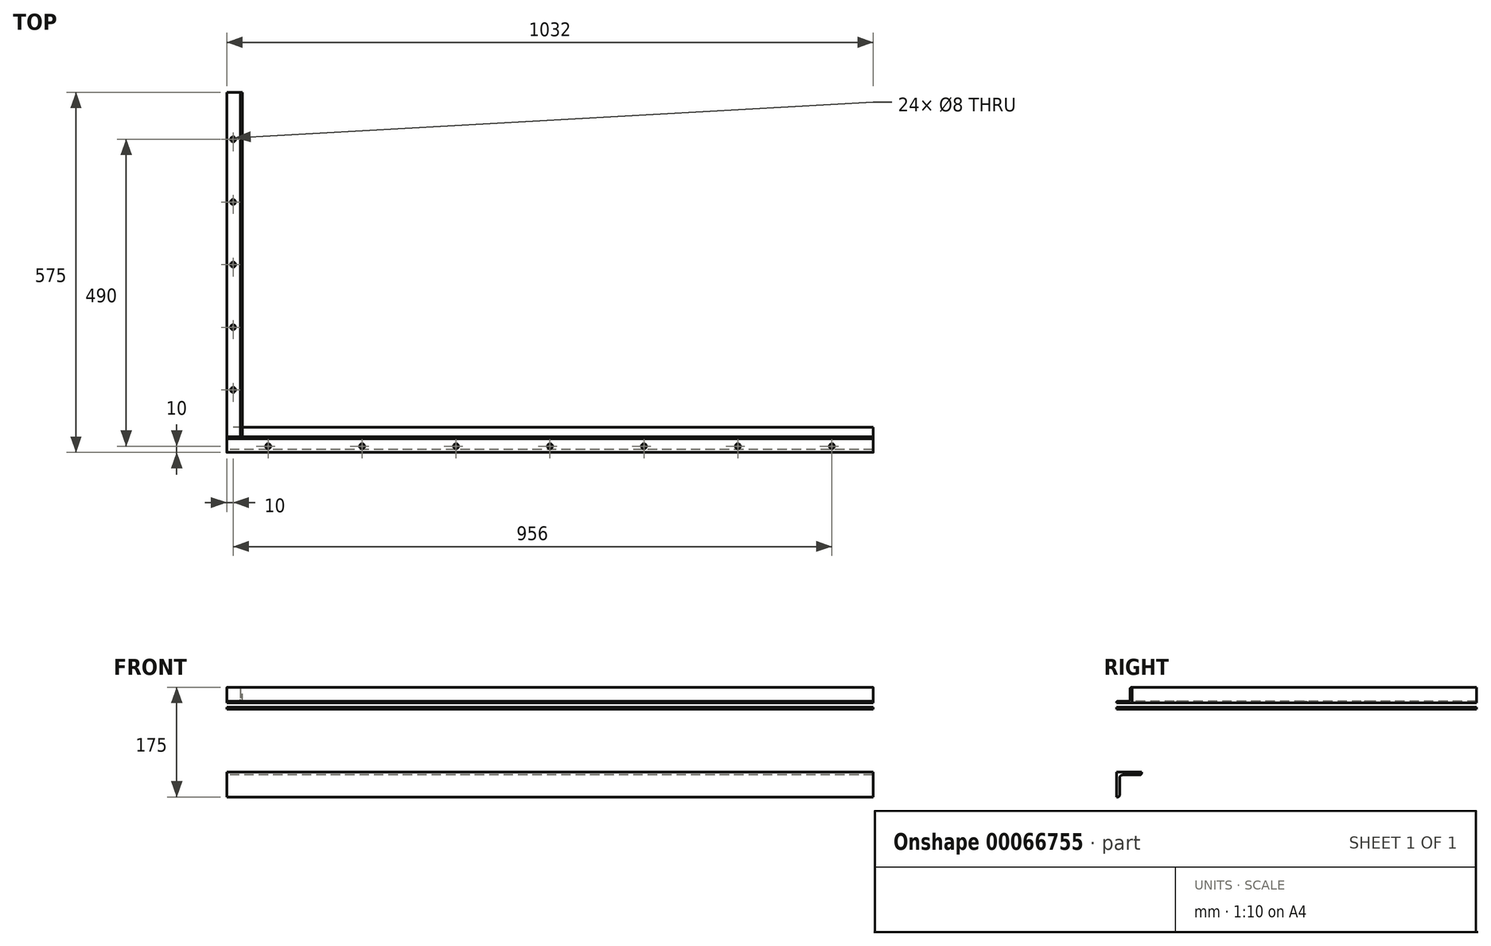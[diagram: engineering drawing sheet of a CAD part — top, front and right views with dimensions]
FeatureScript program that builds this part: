
annotation { "Feature Type Name" : "Feature", "Feature Type Description" : "" }
export const myFeature = defineFeature(function(context is Context, id is Id, definition is map)
    precondition{}
    {
        {
            assignVariable(context, id + "F0", {"name" : "E1", "anyValue" : 1032});
        }
        {
            assignVariable(context, id + "F1", {"name" : "E5", "anyValue" : 550});
        }
        {
            var Q0;
            Q0=qCreatedBy(makeId("Top.planeOp"),FACE);
            var sketch = newSketch(context, id + "F2", { "sketchPlane" : qUnion([Q0])});
            skLineSegment(sketch, "E0.bottom", {"start": v(-516, 0) * mm, "end": v(516, 0) * mm});
            skLineSegment(sketch, "E0.top", {"start": v(-516, -25) * mm, "end": v(516, -25) * mm});
            skLineSegment(sketch, "E0.left", {"start": v(-516, 0) * mm, "end": v(-516, -25) * mm});
            skLineSegment(sketch, "E0.right", {"start": v(516, 0) * mm, "end": v(516, -25) * mm});
            skLineSegment(sketch, "E1.bottom", {"start": v(-516, 550) * mm, "end": v(-491, 550) * mm});
            skLineSegment(sketch, "E1.top", {"start": v(-516, 0) * mm, "end": v(-491, 0) * mm});
            skLineSegment(sketch, "E1.left", {"start": v(-516, 550) * mm, "end": v(-516, 0) * mm});
            skLineSegment(sketch, "E1.right", {"start": v(-491, 550) * mm, "end": v(-491, 0) * mm});
            skSolve(sketch);
        }
        {
            var Q0;
            Q0=qCreatedBy(makeId("Right.planeOp"),FACE);
            var sketch = newSketch(context, id + "F3", { "sketchPlane" : qUnion([Q0])});
            skLineSegment(sketch, "E2", {"start": v(-25, 10) * mm, "end": v(0, 10) * mm});
            skLineSegment(sketch, "E3", {"start": v(0, 10) * mm, "end": v(0, 35) * mm});
            skLineSegment(sketch, "E4", {"start": v(0, 35) * mm, "end": v(-1, 35) * mm});
            skLineSegment(sketch, "E5", {"start": v(-3, 33) * mm, "end": v(-3, 16) * mm});
            skLineSegment(sketch, "E6", {"start": v(-6, 13) * mm, "end": v(-23, 13) * mm});
            skLineSegment(sketch, "E7", {"start": v(-25, 11) * mm, "end": v(-25, 10) * mm});
            skPoint(sketch, "E8.visualSharp", {"position": v(-3, 35) * mm});
            skArc(sketch, "E8.filletArc", {"start": v(-1, 35) * mm, "mid": v(-2.41, 34.41) * mm, "end": v(-3, 33) * mm});
            skPoint(sketch, "E9.visualSharp", {"position": v(-25, 13) * mm});
            skArc(sketch, "E9.filletArc", {"start": v(-23, 13) * mm, "mid": v(-24.41, 12.41) * mm, "end": v(-25, 11) * mm});
            skPoint(sketch, "E10.visualSharp", {"position": v(-3, 13) * mm});
            skArc(sketch, "E10.filletArc", {"start": v(-6, 13) * mm, "mid": v(-3.88, 13.88) * mm, "end": v(-3, 16) * mm});
            skSolve(sketch);
        }
        {
            var Q0;
            Q0=makeQuery(id+"F2.imprint","IMPRINT",FACE,{"disambiguationData":[TD([[makeQuery(id+"F2.imprint","IMPRINT",EDGE,{"derivedFrom":sQuery(id+"F2.wireOp",EDGE,"E0.bottom")}),-1.0]])]});
            extrude(context, id + "F4", {"entities" : qUnion([Q0]), "depth" : 3 * mm});
        }
        {
            var Q0;
            Q0=makeQuery(id+"F2.imprint","IMPRINT",FACE,{"disambiguationData":[TD([[makeQuery(id+"F2.imprint","IMPRINT",EDGE,{"derivedFrom":sQuery(id+"F2.wireOp",EDGE,"E1.bottom")}),-1.0]])]});
            extrude(context, id + "F5", {"entities" : qUnion([Q0]), "depth" : 3 * mm});
        }
        {
            var Q0;
            Q0=makeQuery(id+"F4.opExtrude","CAP_FACE",FACE,{"disambiguationData":[OSD([sQuery(id+"F2.wireOp",EDGE,"E0.bottom"),sQuery(id+"F2.wireOp",EDGE,"E0.top"),sQuery(id+"F2.wireOp",EDGE,"E0.left"),sQuery(id+"F2.wireOp",EDGE,"E0.right")])],"isStart":false});
            var sketch = newSketch(context, id + "F6", { "sketchPlane" : qUnion([Q0])});
            skCircle(sketch, "E11", {"center": v(-450, -15) * mm, "radius": 4 * mm});
            skCircle(sketch, "E12.1.0.0", {"center": v(-300, -15) * mm, "radius": 4 * mm});
            skCircle(sketch, "E12.2.0.0", {"center": v(-150, -15) * mm, "radius": 4 * mm});
            skCircle(sketch, "E12.3.0.0", {"center": v(0, -15) * mm, "radius": 4 * mm});
            skCircle(sketch, "E12.4.0.0", {"center": v(150, -15) * mm, "radius": 4 * mm});
            skCircle(sketch, "E12.5.0.0", {"center": v(300, -15) * mm, "radius": 4 * mm});
            skCircle(sketch, "E12.6.0.0", {"center": v(450, -15) * mm, "radius": 4 * mm});
            skLineSegment(sketch, "E12.direction1", {"start": v(-450, -15) * mm, "end": v(-300, -15) * mm, "construction": true});
            skSolve(sketch);
        }
        {
            var Q0;
            Q0=makeQuery(id+"F3.imprint","IMPRINT",FACE,{"disambiguationData":[TD([[makeQuery(id+"F3.imprint","IMPRINT",EDGE,{"derivedFrom":sQuery(id+"F3.wireOp",EDGE,"E2")}),1.0]])]});
            extrude(context, id + "F7", {"entities" : qUnion([Q0]), "depth" : (getVariable(context, 'E1')) * mm, "symmetric" : true});
        }
        {
            var Q0;
            Q0 = qSketchRegion(id + "F6", true);
            extrude(context, id + "F8", {"entities" : qUnion([Q0]), "operationType" : NewBodyOperationType.REMOVE, "endBound" : BoundingType.THROUGH_ALL, "oppositeDirection" : true, "depth" : 25 * mm});
        }
        {
            var Q0;
            Q0 = qSketchRegion(id + "F6", true);
            extrude(context, id + "F9", {"entities" : qUnion([Q0]), "operationType" : NewBodyOperationType.REMOVE, "endBound" : BoundingType.THROUGH_ALL, "depth" : 25 * mm});
        }
        {
            var Q0;
            Q0=qCreatedBy(makeId("Front.planeOp"),FACE);
            var sketch = newSketch(context, id + "F10", { "sketchPlane" : qUnion([Q0])});
            skLineSegment(sketch, "E13", {"start": v(-491, 10) * mm, "end": v(-491, 35) * mm});
            skLineSegment(sketch, "E14", {"start": v(-491, 35) * mm, "end": v(-492, 35) * mm});
            skLineSegment(sketch, "E15", {"start": v(-494, 33) * mm, "end": v(-494, 16) * mm});
            skLineSegment(sketch, "E16", {"start": v(-497, 13) * mm, "end": v(-514, 13) * mm});
            skLineSegment(sketch, "E17", {"start": v(-516, 11) * mm, "end": v(-516, 10) * mm});
            skLineSegment(sketch, "E18", {"start": v(-516, 10) * mm, "end": v(-491, 10) * mm});
            skPoint(sketch, "E19.visualSharp", {"position": v(-494, 35) * mm});
            skArc(sketch, "E19.filletArc", {"start": v(-492, 35) * mm, "mid": v(-493.41, 34.41) * mm, "end": v(-494, 33) * mm});
            skPoint(sketch, "E20.visualSharp", {"position": v(-516, 13) * mm});
            skArc(sketch, "E20.filletArc", {"start": v(-514, 13) * mm, "mid": v(-515.41, 12.41) * mm, "end": v(-516, 11) * mm});
            skPoint(sketch, "E21.visualSharp", {"position": v(-494, 13) * mm});
            skArc(sketch, "E21.filletArc", {"start": v(-497, 13) * mm, "mid": v(-494.88, 13.88) * mm, "end": v(-494, 16) * mm});
            skSolve(sketch);
        }
        {
            var Q0;
            Q0=makeQuery(id+"F5.opExtrude","CAP_FACE",FACE,{"disambiguationData":[OSD([sQuery(id+"F2.wireOp",EDGE,"E1.bottom"),sQuery(id+"F2.wireOp",EDGE,"E1.top"),sQuery(id+"F2.wireOp",EDGE,"E1.left"),sQuery(id+"F2.wireOp",EDGE,"E1.right")])],"isStart":false});
            var sketch = newSketch(context, id + "F11", { "sketchPlane" : qUnion([Q0])});
            skCircle(sketch, "E22", {"center": v(-506, 75) * mm, "radius": 4 * mm});
            skCircle(sketch, "E23.0.1.0", {"center": v(-506, 175) * mm, "radius": 4 * mm});
            skCircle(sketch, "E23.0.2.0", {"center": v(-506, 275) * mm, "radius": 4 * mm});
            skCircle(sketch, "E23.0.3.0", {"center": v(-506, 375) * mm, "radius": 4 * mm});
            skCircle(sketch, "E23.0.4.0", {"center": v(-506, 475) * mm, "radius": 4 * mm});
            skLineSegment(sketch, "E23.direction1", {"start": v(-506, 75) * mm, "end": v(-481, 75) * mm, "construction": true});
            skLineSegment(sketch, "E23.direction2", {"start": v(-506, 75) * mm, "end": v(-506, 175) * mm, "construction": true});
            skSolve(sketch);
        }
        {
            var Q0;
            Q0 = qSketchRegion(id + "F11", true);
            extrude(context, id + "F12", {"entities" : qUnion([Q0]), "operationType" : NewBodyOperationType.REMOVE, "endBound" : BoundingType.THROUGH_ALL, "oppositeDirection" : true, "depth" : 25 * mm});
        }
        {
            var Q0;
            Q0=makeQuery(id+"F10.imprint","IMPRINT",FACE,{"disambiguationData":[TD([[makeQuery(id+"F10.imprint","IMPRINT",EDGE,{"derivedFrom":sQuery(id+"F10.wireOp",EDGE,"E13")}),1.0]])]});
            extrude(context, id + "F13", {"entities" : qUnion([Q0]), "oppositeDirection" : true, "depth" : (getVariable(context, 'E5')) * mm});
        }
        {
            var Q0;
            Q0 = qSketchRegion(id + "F11", true);
            extrude(context, id + "F14", {"entities" : qUnion([Q0]), "operationType" : NewBodyOperationType.REMOVE, "endBound" : BoundingType.THROUGH_ALL, "depth" : 25 * mm});
        }
        {
            var Q0;
            Q0=qCreatedBy(makeId("Right.planeOp"),FACE);
            var sketch = newSketch(context, id + "F15", { "sketchPlane" : qUnion([Q0])});
            skLineSegment(sketch, "E24", {"start": v(15, -100) * mm, "end": v(-25, -100) * mm});
            skLineSegment(sketch, "E25", {"start": v(-25, -100) * mm, "end": v(-25, -140) * mm});
            skLineSegment(sketch, "E26", {"start": v(-25, -140) * mm, "end": v(-23, -140) * mm});
            skLineSegment(sketch, "E27", {"start": v(-20, -137) * mm, "end": v(-20, -110) * mm});
            skLineSegment(sketch, "E28", {"start": v(-15, -105) * mm, "end": v(12, -105) * mm});
            skLineSegment(sketch, "E29", {"start": v(15, -102) * mm, "end": v(15, -100) * mm});
            skPoint(sketch, "E30.visualSharp", {"position": v(15, -105) * mm});
            skArc(sketch, "E30.filletArc", {"start": v(12, -105) * mm, "mid": v(14.12, -104.12) * mm, "end": v(15, -102) * mm});
            skPoint(sketch, "E31.visualSharp", {"position": v(-20, -140) * mm});
            skArc(sketch, "E31.filletArc", {"start": v(-23, -140) * mm, "mid": v(-20.88, -139.12) * mm, "end": v(-20, -137) * mm});
            skPoint(sketch, "E32.visualSharp", {"position": v(-20, -105) * mm});
            skArc(sketch, "E32.filletArc", {"start": v(-15, -105) * mm, "mid": v(-18.54, -106.46) * mm, "end": v(-20, -110) * mm});
            skSolve(sketch);
        }
        {
            var Q0;
            Q0=makeQuery(id+"F15.imprint","IMPRINT",FACE,{"disambiguationData":[TD([[makeQuery(id+"F15.imprint","IMPRINT",EDGE,{"derivedFrom":sQuery(id+"F15.wireOp",EDGE,"E24")}),1.0]])]});
            extrude(context, id + "F16", {"entities" : qUnion([Q0]), "depth" : (getVariable(context, 'E1')) * mm, "symmetric" : true});
        }
    });
